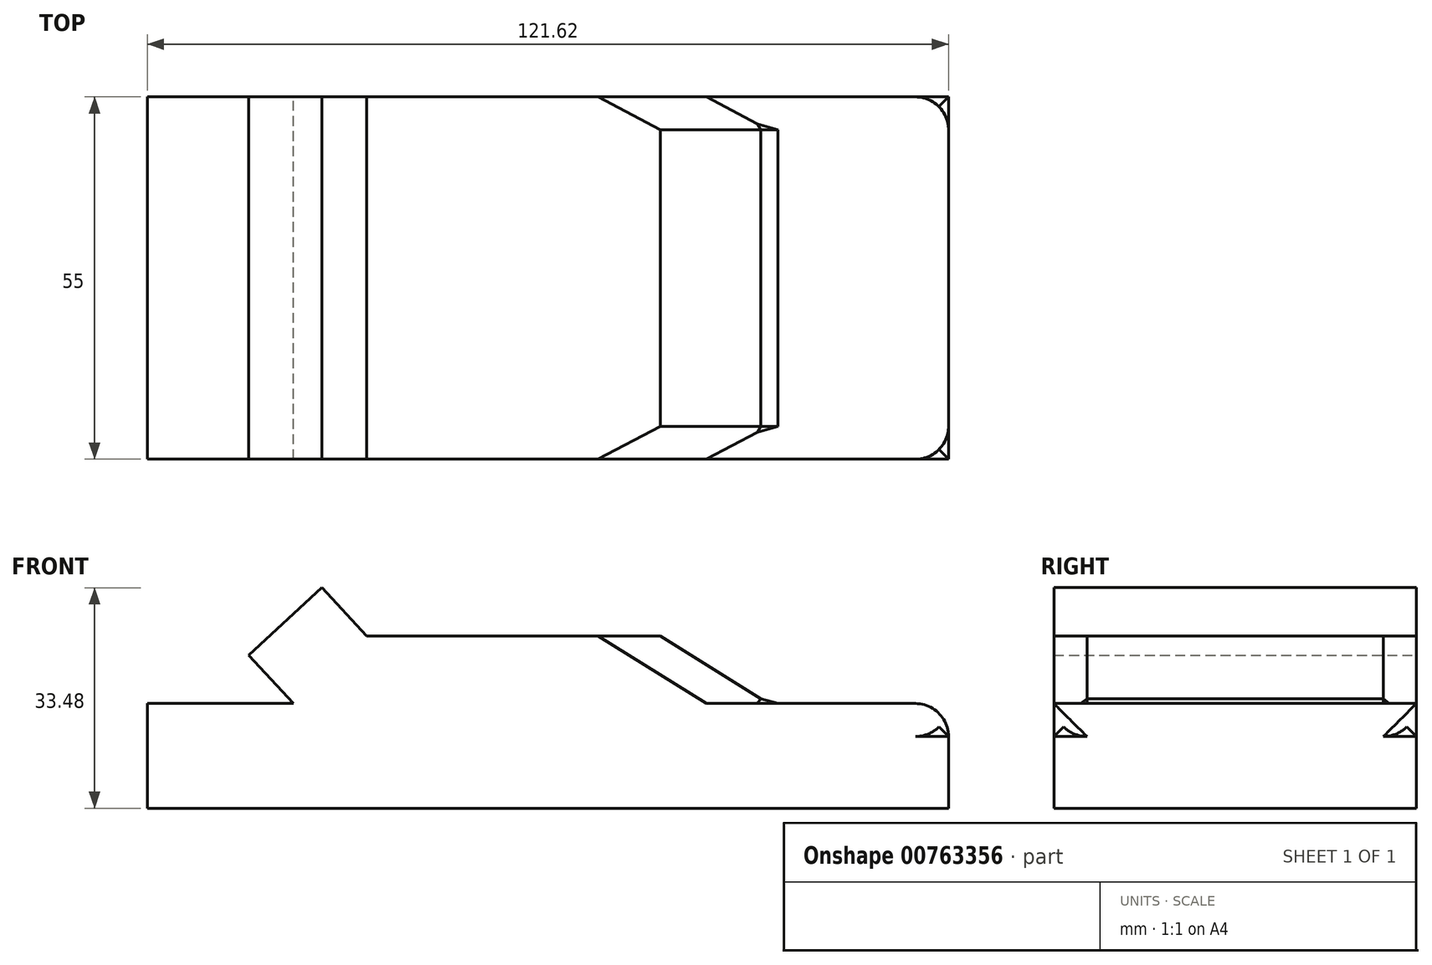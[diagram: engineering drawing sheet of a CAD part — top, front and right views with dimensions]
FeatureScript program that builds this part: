
annotation { "Feature Type Name" : "Feature", "Feature Type Description" : "" }
export const myFeature = defineFeature(function(context is Context, id is Id, definition is map)
    precondition{}
    {
        {
            var Q0;
            Q0=qCreatedBy(makeId("Front.planeOp"),FACE);
            var sketch = newSketch(context, id + "F0", { "sketchPlane" : qUnion([Q0])});
            skLineSegment(sketch, "E0.bottom", {"start": v(-56, 0) * mm, "end": v(65.6, 0) * mm});
            skLineSegment(sketch, "E0.top", {"start": v(-56, 15.9) * mm, "end": v(65.6, 15.9) * mm});
            skLineSegment(sketch, "E0.left", {"start": v(-56, 0) * mm, "end": v(-56, 15.9) * mm});
            skLineSegment(sketch, "E0.right", {"start": v(65.6, 0) * mm, "end": v(65.6, 15.9) * mm});
            skLineSegment(sketch, "E1.bottom", {"start": v(-29.34, 15.9) * mm, "end": v(33.4, 15.9) * mm});
            skLineSegment(sketch, "E1.top", {"start": v(-22.72, 26.14) * mm, "end": v(21.87, 26.14) * mm});
            skLineSegment(sketch, "E2", {"start": v(21.87, 26.14) * mm, "end": v(38.3, 15.9) * mm});
            skLineSegment(sketch, "E3", {"start": v(-22.72, 26.14) * mm, "end": v(-33.82, 15.9) * mm});
            skSolve(sketch);
        }
        {
            var Q0;
            Q0=makeQuery(id+"F0.imprint","IMPRINT",FACE,{"disambiguationData":[TD([[makeQuery(id+"F0.imprint","IMPRINT",EDGE,{"derivedFrom":sQuery(id+"F0.wireOp",EDGE,"E0.bottom")}),1.0]])]});
            var sketch = newSketch(context, id + "F1", { "sketchPlane" : qUnion([Q0])});
            skArc(sketch, "E4", {"start": v(58.6, 0) * mm, "mid": v(51.67, 6.58) * mm, "end": v(44.74, 0) * mm});
            skArc(sketch, "E5", {"start": v(-37.42, 0) * mm, "mid": v(-43.83, 7.2) * mm, "end": v(-50.24, 0) * mm});
            skSolve(sketch);
        }
        {
            var Q0;
            {var subQ9=sQuery(id+"F1.wireOp",EDGE,"E4");Q0=makeQuery(id+"F1.imprint","IMPRINT",FACE,{"disambiguationData":[TD([[makeQuery(id+"F1.imprint","IMPRINT",EDGE,{"derivedFrom":subQ9}),-1.0]])]});}
            var Q1;
            Q1=makeQuery(id+"F0.imprint","IMPRINT",FACE,{"disambiguationData":[TD([[makeQuery(id+"F0.imprint","IMPRINT",EDGE,{"derivedFrom":sQuery(id+"F0.wireOp",EDGE,"E0.bottom")}),1.0]])]});
            var Q2;
            Q2=makeQuery(id+"F0.imprint","IMPRINT",FACE,{"disambiguationData":[TD([[makeQuery(id+"F0.imprint","IMPRINT",EDGE,{"derivedFrom":sQuery(id+"F0.wireOp",EDGE,"E1.top")}),-1.0]])]});
            extrude(context, id + "F2", {"entities" : qUnion([Q0, Q1, Q2]), "depth" : 55 * mm, "offsetDistance" : 25 * mm});
        }
        {
            var Q0;
            {var subQ0=sQuery(id+"F0.wireOp",EDGE,"E0.top");Q0=makeQuery(id+"F2.opExtrude","SWEPT_FACE",FACE,{"disambiguationData":[OSD([subQ0]),TDD([makeQuery(id+"F0.imprint","IMPRINT",EDGE,{"disambiguationData":[TD([[makeQuery(id+"F0.imprint","INTERSECT",VERTEX,{"derivedFrom":[subQ0,sQuery(id+"F0.wireOp",EDGE,"E0.right")]}),1.0]])],"derivedFrom":subQ0})])]});}
            chamfer(context, id + "F3", {"entities" : qUnion([Q0]), "width" : 5 * mm, "tangentPropagation" : true});
        }
        {
            var Q0;
            {var subQ0=sQuery(id+"F0.wireOp",EDGE,"E0.right");Q0=makeQuery(id+"F2.opExtrude","SWEPT_FACE",FACE,{"disambiguationData":[OSD([subQ0]),TDD([makeQuery(id+"F1.imprint","IMPRINT",EDGE,{"derivedFrom":makeQuery(id+"F0.imprint","IMPRINT",EDGE,{"derivedFrom":subQ0})})])]});}
            fillet(context, id + "F4", {"entities" : qUnion([Q0]), "radius" : 5 * mm, "tangentPropagation" : true, "allowEdgeOverflow" : false});
        }
        {
            var Q0;
            Q0=makeQuery(id+"F2.opExtrude","SWEPT_FACE",FACE,{"disambiguationData":[OSD([sQuery(id+"F0.wireOp",EDGE,"E3")])]});
            extrude(context, id + "F5", {"entities" : qUnion([Q0]), "operationType" : NewBodyOperationType.ADD, "depth" : 10 * mm, "offsetDistance" : 25 * mm});
        }
    });
